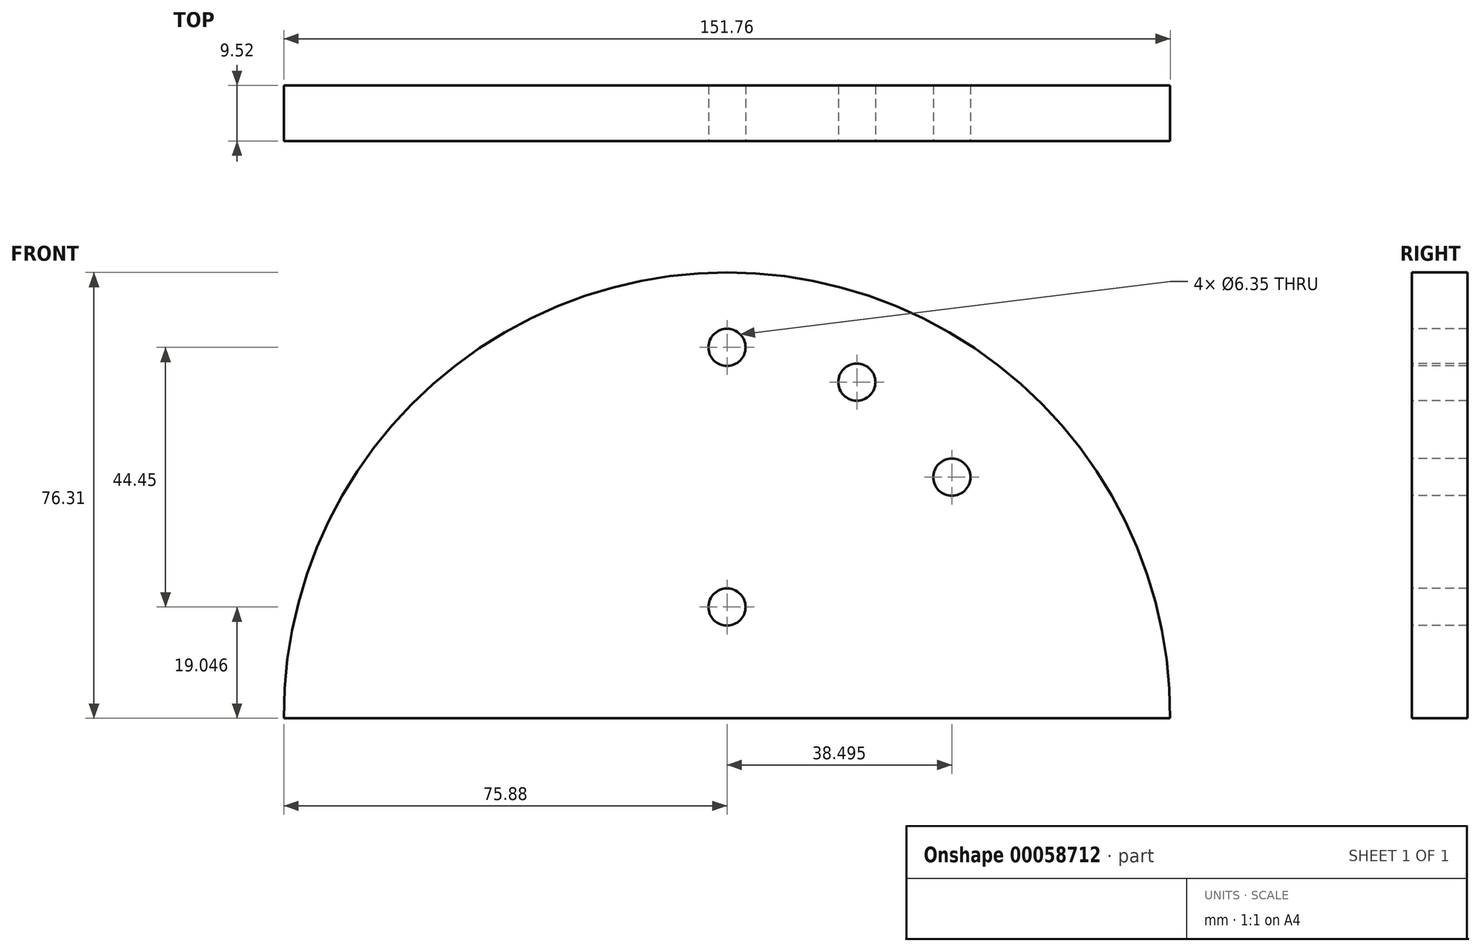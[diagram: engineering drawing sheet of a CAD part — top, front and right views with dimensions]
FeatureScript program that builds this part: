
annotation { "Feature Type Name" : "Feature", "Feature Type Description" : "" }
export const myFeature = defineFeature(function(context is Context, id is Id, definition is map)
    precondition{}
    {
        {
            var Q0;
            Q0=qCreatedBy(makeId("Front.planeOp"),FACE);
            var sketch = newSketch(context, id + "F0", { "sketchPlane" : qUnion([Q0])});
            skLineSegment(sketch, "E0", {"start": v(-75.88, -0.43) * mm, "end": v(76.52, -0.43) * mm});
            skArc(sketch, "E1", {"start": v(-75.88, -0.43) * mm, "mid": v(0, 75.88) * mm, "end": v(75.88, -0.43) * mm});
            skSolve(sketch);
        }
        {
            var Q0;
            Q0 = qSketchRegion(id + "F0", true);
            extrude(context, id + "F1", {"entities" : qUnion([Q0]), "endBound" : BoundingType.SYMMETRIC, "depth" : 9.52 * mm});
        }
        {
            var Q0;
            Q0=makeQuery(id+"F1.opExtrude","CAP_FACE",FACE,{"disambiguationData":[OSD([sQuery(id+"F0.wireOp",EDGE,"E0"),sQuery(id+"F0.wireOp",EDGE,"E1")])],"isStart":false});
            var sketch = newSketch(context, id + "F2", { "sketchPlane" : qUnion([Q0])});
            skCircle(sketch, "E2", {"center": v(0, 18.62) * mm, "radius": 3.18 * mm});
            skCircle(sketch, "E3", {"center": v(0, 63.07) * mm, "radius": 3.18 * mm});
            skCircle(sketch, "E4.1.0", {"center": v(22.22, 57.11) * mm, "radius": 3.18 * mm});
            skCircle(sketch, "E4.2.0", {"center": v(38.5, 40.84) * mm, "radius": 3.18 * mm});
            skLineSegment(sketch, "E4.anchor1", {"start": v(0, 18.62) * mm, "end": v(0, 63.07) * mm, "construction": true});
            skLineSegment(sketch, "E4.anchor2", {"start": v(0, 18.62) * mm, "end": v(38.5, 40.84) * mm, "construction": true});
            skSolve(sketch);
        }
        {
            var Q0;
            Q0=sQuery(id+"F2.wireOp",VERTEX,"E2.center");
            var Q1;
            Q1=sQuery(id+"F2.wireOp",VERTEX,"E4.anchor2.end");
            var Q2;
            Q2=sQuery(id+"F2.wireOp",VERTEX,"E4.1.0.center");
            var Q3;
            Q3=sQuery(id+"F2.wireOp",VERTEX,"E3.center");
            var Q4;
            Q4=makeQuery(id+"F1.opExtrude","SWEPT_BODY",BODY,{"disambiguationData":[OSD([sQuery(id+"F0.wireOp",EDGE,"E0"),sQuery(id+"F0.wireOp",EDGE,"E1")])]});
            hole(context, id + "F3", {"style" : HoleStyle.SIMPLE, "holeDiameter" : 6.35 * mm, "endStyle" : HoleEndStyle.THROUGH, "locations" : qUnion([Q0, Q1, Q2, Q3]), "scope" : qUnion([Q4])});
        }
    });
